# Revit family: Hager-Orion-IP66-D500-Cl.I-Inox_encl-630A-CH-de
name_source: partatom
category: Electrical Equipment
units: mm (PartAtom-declared; Revit-internal decimal feet)

## family parameters
Cut with Voids When Loaded = No
Host = Face
Panel Configuration = Two Columns, Circuits Across
Part Type = Panelboard
Room Calculation Point = No
Round Connector Dimension = Use Diameter
Shared = No

## types (1)
- Aufputz IP66 B800 H1000 T300  - FL042BWL
    Default Elevation = 0 mm  [stored 0 ft]
    EF000003 - Montageart = EV000384 - Aufputz
    EF000007 - Farbe = EV000154 - sonstige
    EF000008 - Breite = 800 mm  [stored 2.62467 ft]
    EF000040 - Höhe = 1000 mm  [stored 3.28084 ft]
    EF000049 - Tiefe = 300 mm
    EF000118 - Mit Montageplatte = No
    EF000218 - Einbautiefe = 0 mm  [stored 0 ft]
    EF000266 - Anzahl der Reihen = 0
    EF000339 - Art der Abdeckung = EV004216 - Tür
    EF000437 - Anzahl der Leitungseinführungen = 0
    EF001088 - Anbaumöglichkeit = Yes
    EF001131 - Innentiefe = 266 mm
    EF001596 - Werkstoff des Gehäuses = EV000166 - rostfreier Stahl
    EF002950 - Breite in Teilungseinheiten = 0
    EF003532 - Geeignet für Außengebrauch = Yes
    EF004293 - Schlagfestigkeit = EV008784 - IK10
    EF004427 - Anzahl der Module = 0
    EF004464 - Art der Tür = EV002646 - Einzel
    EF005474 - Schutzart (IP) = EV006422 - IP66
    EF006244 - Transparenter Deckel/Tür = No
    EF006306 - Mit Schloss = No
    EF007800 - Geeignet für Blitzschutz = No
    EF008873 - Nennstrom (In) = 630 A
    EF009170 - Materialstärke Gehäuse = 2 mm  [stored 0.00656168 ft]
    EF009171 - Materialstärke Tür/Deckel = 2 mm  [stored 0.00656168 ft]
    EF009212 - Ausführung Deckel = EV009916 - mit Ausschnitt
    EF009554 - Anzahl der Öffnungen für Flanschplatten = 0
    EF015940 - Deckel mit Überdruckentlastung = No
    HG000002 - Mit tür = Yes
    HG000003 - Bereich = Orion
    HG000004 - Herstellerreferenz = FL042BWL
    HG000006 - Unterputz = No
    HG000009 - Doppelflügeligen Tür = Yes
    HG000010 - Asymmetrische Türen = Yes
    HG000023 - Gehäuse mit doppeltem Querschnitt = No
    HG000024 - Höhe des unteren Teils = 800 mm  [stored 2.62467 ft]
    HG000026 - Stehend auf dem Boden = No
    HG000027 - Sockelhöhe = 0 mm  [stored 0 ft]
    Manufacturer = Hager
    Type Comments = Orion

note: [stored X ft] marks values corroborated as IEEE doubles in the binary element streams (Revit-internal decimal feet)

## geometry (parser evidence)
native form markers: Sweep x6
no freeform markers — native parametric forms only
